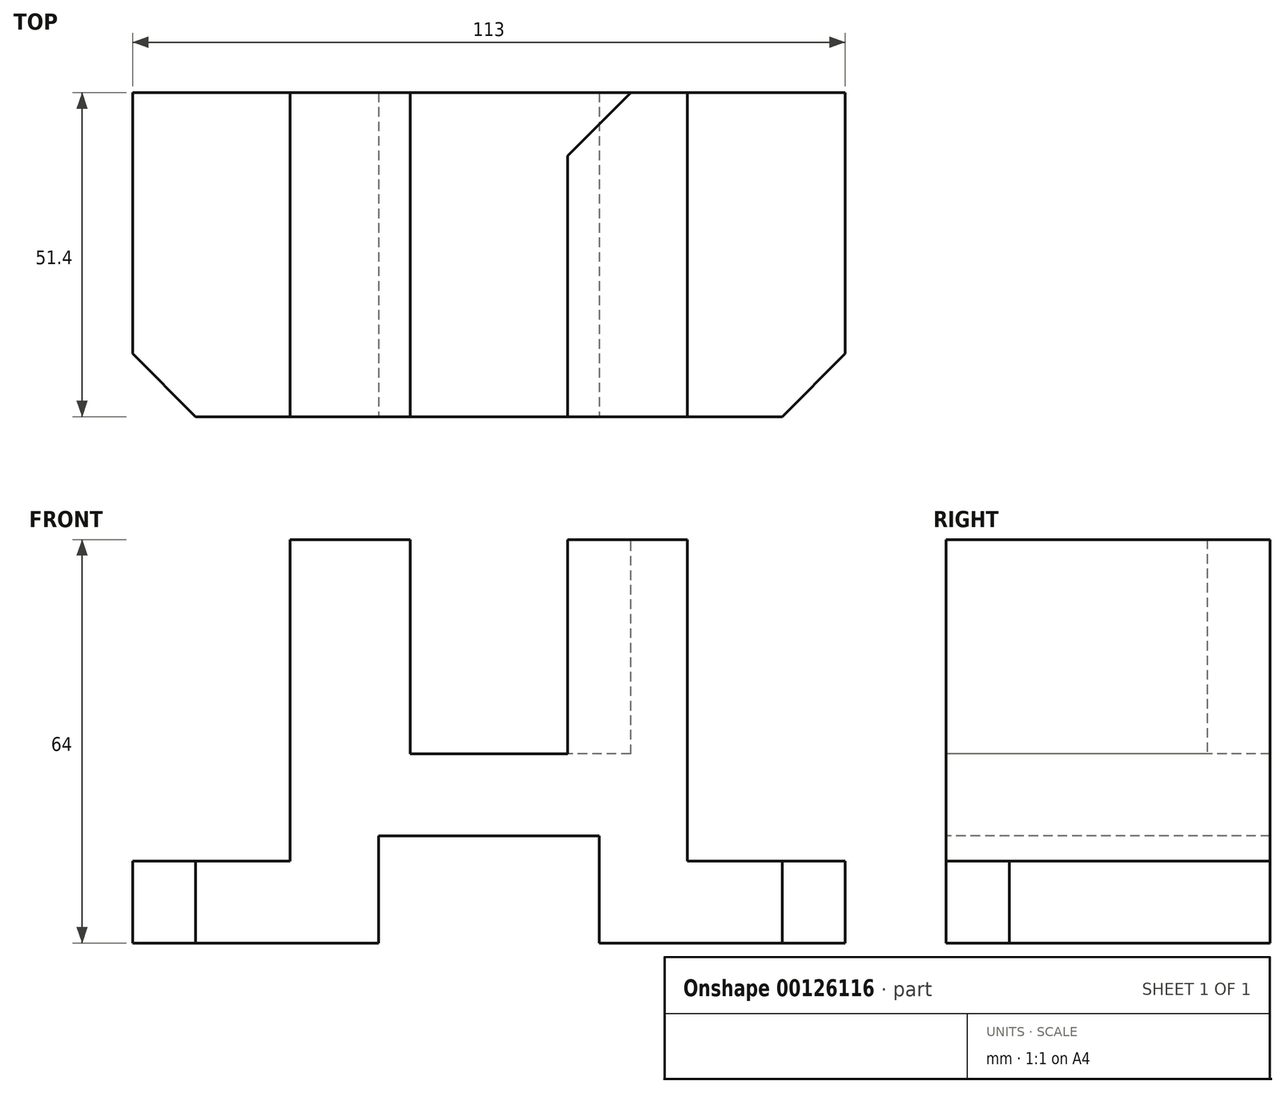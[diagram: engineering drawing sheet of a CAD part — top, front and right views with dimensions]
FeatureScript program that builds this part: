
annotation { "Feature Type Name" : "Feature", "Feature Type Description" : "" }
export const myFeature = defineFeature(function(context is Context, id is Id, definition is map)
    precondition{}
    {
        {
            var Q0;
            Q0=qCreatedBy(makeId("Top.planeOp"),FACE);
            var sketch = newSketch(context, id + "F0", { "sketchPlane" : qUnion([Q0])});
            skLineSegment(sketch, "E0.bottom", {"start": v(-51, 24.77) * mm, "end": v(62, 24.77) * mm});
            skLineSegment(sketch, "E0.top", {"start": v(-51, -1.23) * mm, "end": v(62, -1.23) * mm});
            skLineSegment(sketch, "E0.left", {"start": v(-51, 24.77) * mm, "end": v(-51, -1.23) * mm});
            skLineSegment(sketch, "E0.right", {"start": v(62, 24.77) * mm, "end": v(62, -1.23) * mm});
            skSolve(sketch);
        }
        {
            var Q0;
            Q0 = qSketchRegion(id + "F0", true);
            extrude(context, id + "F1", {"entities" : qUnion([Q0]), "depth" : 64 * mm});
        }
        {
            var Q0;
            Q0=qCreatedBy(makeId("Front.planeOp"),FACE);
            var sketch = newSketch(context, id + "F2", { "sketchPlane" : qUnion([Q0])});
            skLineSegment(sketch, "E1.bottom", {"start": v(-7, 66.5) * mm, "end": v(18, 66.5) * mm});
            skLineSegment(sketch, "E1.top", {"start": v(-7, 30) * mm, "end": v(18, 30) * mm});
            skLineSegment(sketch, "E1.left", {"start": v(-7, 66.5) * mm, "end": v(-7, 30) * mm});
            skLineSegment(sketch, "E1.right", {"start": v(18, 66.5) * mm, "end": v(18, 30) * mm});
            skSolve(sketch);
        }
        {
            var Q0;
            Q0 = qSketchRegion(id + "F2", true);
            extrude(context, id + "F3", {"entities" : qUnion([Q0]), "operationType" : NewBodyOperationType.REMOVE, "endBound" : BoundingType.SYMMETRIC, "oppositeDirection" : true, "depth" : 101.6 * mm});
        }
        {
            var Q0;
            Q0=qCreatedBy(makeId("Front.planeOp"),FACE);
            var sketch = newSketch(context, id + "F4", { "sketchPlane" : qUnion([Q0])});
            skLineSegment(sketch, "E2.bottom", {"start": v(-51, 13) * mm, "end": v(-26, 13) * mm});
            skLineSegment(sketch, "E2.top", {"start": v(-51, 78.5) * mm, "end": v(-26, 78.5) * mm});
            skLineSegment(sketch, "E2.left", {"start": v(-51, 13) * mm, "end": v(-51, 78.5) * mm});
            skLineSegment(sketch, "E2.right", {"start": v(-26, 13) * mm, "end": v(-26, 78.5) * mm});
            skSolve(sketch);
        }
        {
            var Q0;
            Q0 = qSketchRegion(id + "F4", true);
            extrude(context, id + "F5", {"entities" : qUnion([Q0]), "operationType" : NewBodyOperationType.REMOVE, "endBound" : BoundingType.SYMMETRIC, "depth" : 101.6 * mm});
        }
        {
            var Q0;
            Q0=makeQuery(id+"F1.opExtrude","SWEPT_FACE",FACE,{"disambiguationData":[OSD([sQuery(id+"F0.wireOp",EDGE,"E0.top")])]});
            var Q1;
            Q1=makeQuery(id+"F1.opExtrude","SWEPT_FACE",FACE,{"disambiguationData":[OSD([sQuery(id+"F0.wireOp",EDGE,"E0.bottom")])]});
            extrude(context, id + "F6", {"entities" : qUnion([Q0, Q1]), "operationType" : NewBodyOperationType.ADD, "depth" : 25.4 * mm});
        }
        {
            var Q0;
            Q0=qCreatedBy(makeId("Front.planeOp"),FACE);
            var sketch = newSketch(context, id + "F7", { "sketchPlane" : qUnion([Q0])});
            skLineSegment(sketch, "E3.bottom", {"start": v(62, 13) * mm, "end": v(37, 13) * mm});
            skLineSegment(sketch, "E3.top", {"start": v(62, 67.85) * mm, "end": v(37, 67.85) * mm});
            skLineSegment(sketch, "E3.left", {"start": v(62, 13) * mm, "end": v(62, 67.85) * mm});
            skLineSegment(sketch, "E3.right", {"start": v(37, 13) * mm, "end": v(37, 67.85) * mm});
            skSolve(sketch);
        }
        {
            var Q0;
            Q0 = qSketchRegion(id + "F7", true);
            extrude(context, id + "F8", {"entities" : qUnion([Q0]), "operationType" : NewBodyOperationType.REMOVE, "endBound" : BoundingType.SYMMETRIC, "oppositeDirection" : true, "depth" : 101.6 * mm});
        }
        {
            var Q0;
            Q0=qCreatedBy(makeId("Front.planeOp"),FACE);
            var sketch = newSketch(context, id + "F9", { "sketchPlane" : qUnion([Q0])});
            skLineSegment(sketch, "E4.bottom", {"start": v(-12, 0) * mm, "end": v(23, 0) * mm});
            skLineSegment(sketch, "E4.top", {"start": v(-12, 17) * mm, "end": v(23, 17) * mm});
            skLineSegment(sketch, "E4.left", {"start": v(-12, 0) * mm, "end": v(-12, 17) * mm});
            skLineSegment(sketch, "E4.right", {"start": v(23, 0) * mm, "end": v(23, 17) * mm});
            skSolve(sketch);
        }
        {
            var Q0;
            Q0 = qSketchRegion(id + "F9", true);
            extrude(context, id + "F10", {"entities" : qUnion([Q0]), "operationType" : NewBodyOperationType.REMOVE, "endBound" : BoundingType.SYMMETRIC, "oppositeDirection" : true, "depth" : 101.6 * mm});
        }
        {
            var Q0;
            Q0=makeQuery(id+"F6.opExtrude","CAP_EDGE",EDGE,{"disambiguationData":[OSD([sQuery(id+"F0.wireOp",EDGE,"E0.top"),sQuery(id+"F0.wireOp",EDGE,"E0.right")])],"isStart":false});
            chamfer(context, id + "F11", {"entities" : qUnion([Q0]), "width" : 10 * mm, "tangentPropagation" : true});
        }
        {
            var Q0;
            Q0=makeQuery(id+"F6.opExtrude","CAP_EDGE",EDGE,{"disambiguationData":[OSD([sQuery(id+"F0.wireOp",EDGE,"E0.top"),sQuery(id+"F0.wireOp",EDGE,"E0.left")])],"isStart":false});
            chamfer(context, id + "F12", {"entities" : qUnion([Q0]), "width" : 10 * mm, "tangentPropagation" : true});
        }
        {
            var Q0;
            Q0=makeQuery(id+"F6.opExtrude","CAP_EDGE",EDGE,{"disambiguationData":[OSD([sQuery(id+"F0.wireOp",EDGE,"E0.top"),sQuery(id+"F0.wireOp",EDGE,"E0.left")])],"isStart":false});
            var Q1;
            Q1=makeQuery(id+"F3.boolean.opBoolean","INTERSECT",EDGE,{"derivedFrom":[makeQuery(id+"F1.opExtrude","SWEPT_FACE",FACE,{"disambiguationData":[OSD([sQuery(id+"F0.wireOp",EDGE,"E0.bottom")])]}),makeQuery(id+"F3.opExtrude","SWEPT_FACE",FACE,{"disambiguationData":[OSD([sQuery(id+"F2.wireOp",EDGE,"E1.right")])]})]});
            chamfer(context, id + "F13", {"entities" : qUnion([Q0, Q1]), "width" : 10 * mm, "tangentPropagation" : true});
        }
    });
